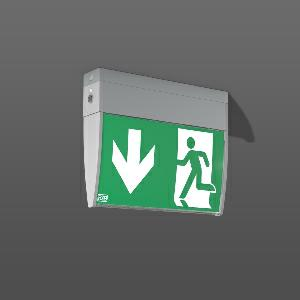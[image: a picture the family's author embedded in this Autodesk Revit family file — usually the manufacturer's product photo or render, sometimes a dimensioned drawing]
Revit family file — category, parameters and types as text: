
# Revit family: gsun_d_671996_004_2_89_72a6
name_source: partatom
category: Lighting Fixtures
units: mm (PartAtom-declared; Revit-internal decimal feet)

## family parameters
Cut with Voids When Loaded = No
Host = Face
Light Source = No
Part Type = Normal
Room Calculation Point = No
Round Connector Dimension = Use Diameter
Shared = No

## types (1)
- GSUN D
    Apparent Load = 0 VA
    Default Elevation = 1800 mm
    Description = Series: GSUN D
Luminaire for escape route identification. Housing: extruded aluminium profile, powder-coated. 4 legends and 1 white lay in plastic sheet included. Universal mounting kit for ceiling and wall surface mounting. Driver integrated. Suitable for connection to central battery systems. With AC Control monitoring module for LUXIFAIR central battery units. 
Colour: silver
Length: 247 mm
Width: 45 mm
Height: 200 mm
Weight: 1 kg
Operating mode: maintained power mode
Viewing Distance: 24 m
Lamp: LED
Socket: without socket
Colour temperature: 4000K
System power: 4.7 W
System power, emergency: 4.7 W
Control gear: Converter not necessary
Protection class: I
Type of protection: IP 30
    Height = 200 mm  [stored 0.656168 ft]
    Lamp = 0 x
    Length = 247 mm
    Luminous efficacy = 0 lm/W
    Manufacturer = RZB
    ModVariant = No
    Model = 671996.004.2.89
    Mounting Place = Ceiling, Wall
    Mounting Type = Surface mounted
    Number of Poles = 1
    OnlyDefault = Yes
    Power Factor = 1
    Product Name = GSUN D
    Product group = Surface mounted ceiling and wall luminaires
    ProductGroupID = 305
    Protection Class = Protection class I
    Protection Degree = IP 30
    RLX_Detail_Level = 1
    RLX_Emergency_Light_Flux = 0 lm
    RLX_Emergency_Type = 0
    RLX_Emergency_Type_DB = No
    RlxData = <blob elided: 30369 chars, md5=ea6e16a9>
    Standby Power = 0 W
    System Light Flux = 0 lm
    System Power = 0 W
    Type Comments = Product without accessories
    Type Image = 671995.004.1.jpg
    URL = http://relux.com
    VarID = ---
    Voltage = 230 V
    Voltage Range = 220-240 V
    Weight = 0.00 kg
    Width = 45 mm

note: [stored X ft] marks values corroborated as IEEE doubles in the binary element streams (Revit-internal decimal feet)

## geometry (parser evidence)
native form markers: Blend x4, Sweep x10
no freeform markers — native parametric forms only
